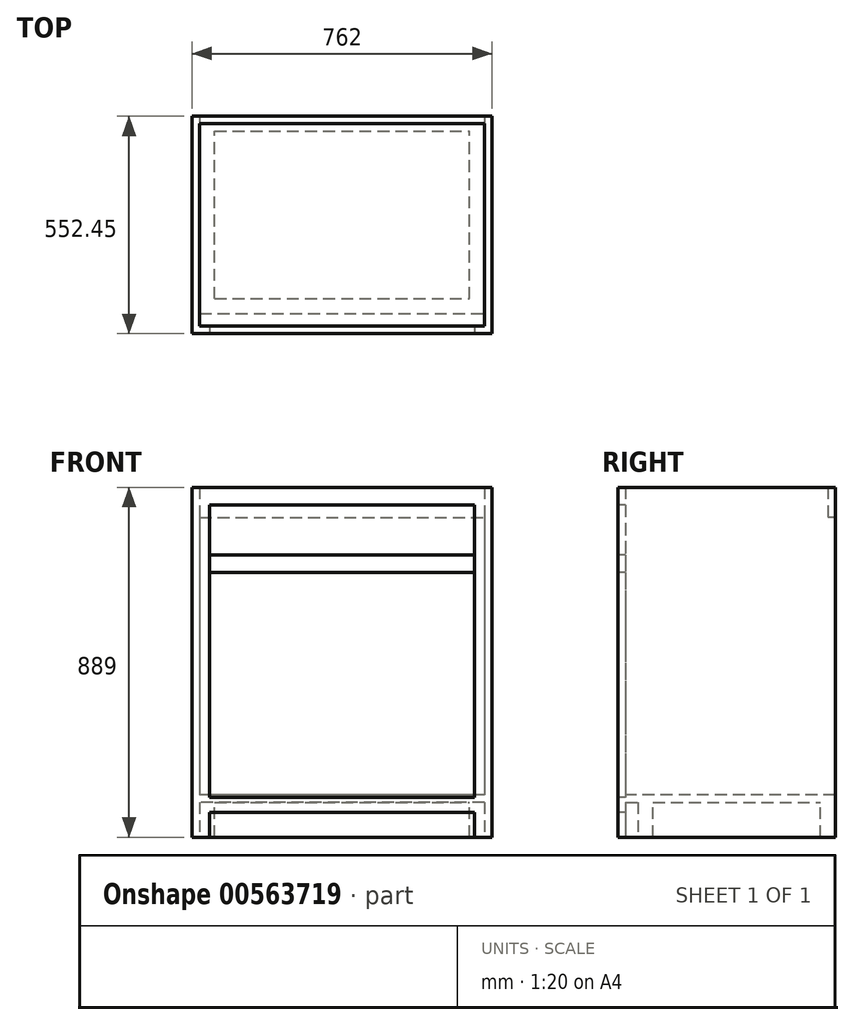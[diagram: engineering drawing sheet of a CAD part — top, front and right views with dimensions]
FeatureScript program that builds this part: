
annotation { "Feature Type Name" : "Feature", "Feature Type Description" : "" }
export const myFeature = defineFeature(function(context is Context, id is Id, definition is map)
    precondition{}
    {
        {
            var Q0;
            Q0=qCreatedBy(makeId("Front.planeOp"),FACE);
            var sketch = newSketch(context, id + "F0", { "sketchPlane" : qUnion([Q0])});
            skLineSegment(sketch, "E0.bottom", {"start": v(-76.53, 47.04) * mm, "end": v(-62.72, 47.04) * mm});
            skLineSegment(sketch, "E0.top", {"start": v(-76.53, -75.78) * mm, "end": v(-62.72, -75.78) * mm});
            skLineSegment(sketch, "E0.left", {"start": v(-76.53, 47.04) * mm, "end": v(-76.53, -75.78) * mm});
            skLineSegment(sketch, "E0.right", {"start": v(-62.72, 47.04) * mm, "end": v(-62.72, -75.78) * mm});
            skLineSegment(sketch, "E1.bottom", {"start": v(-189.83, 884.07) * mm, "end": v(-145.38, 884.07) * mm});
            skLineSegment(sketch, "E1.top", {"start": v(-189.83, -4.93) * mm, "end": v(-145.38, -4.93) * mm});
            skLineSegment(sketch, "E1.left", {"start": v(-189.83, 884.07) * mm, "end": v(-189.83, -4.93) * mm});
            skLineSegment(sketch, "E1.right", {"start": v(-145.38, 884.07) * mm, "end": v(-145.38, -4.93) * mm});
            skLineSegment(sketch, "E2.bottom", {"start": v(527.72, 884.07) * mm, "end": v(572.17, 884.07) * mm});
            skLineSegment(sketch, "E2.top", {"start": v(527.72, -4.93) * mm, "end": v(572.17, -4.93) * mm});
            skLineSegment(sketch, "E2.left", {"start": v(527.72, 884.07) * mm, "end": v(527.72, -4.93) * mm});
            skLineSegment(sketch, "E2.right", {"start": v(572.17, 884.07) * mm, "end": v(572.17, -4.93) * mm});
            skLineSegment(sketch, "E3", {"start": v(-145.38, 884.07) * mm, "end": v(527.72, 884.07) * mm});
            skLineSegment(sketch, "E4", {"start": v(-145.38, 839.62) * mm, "end": v(527.72, 839.62) * mm});
            skLineSegment(sketch, "E5", {"start": v(-145.38, 58.57) * mm, "end": v(527.72, 58.57) * mm});
            skLineSegment(sketch, "E6", {"start": v(-145.38, 96.67) * mm, "end": v(527.72, 96.67) * mm});
            skLineSegment(sketch, "E7.bottom", {"start": v(-145.38, 712.62) * mm, "end": v(527.72, 712.62) * mm});
            skLineSegment(sketch, "E7.top", {"start": v(-145.38, 668.17) * mm, "end": v(527.72, 668.17) * mm});
            skLineSegment(sketch, "E7.left", {"start": v(-145.38, 712.62) * mm, "end": v(-145.38, 668.17) * mm});
            skLineSegment(sketch, "E7.right", {"start": v(527.72, 712.62) * mm, "end": v(527.72, 668.17) * mm});
            skSolve(sketch);
        }
        {
            var Q0;
            {var subQ0=sQuery(id+"F0.wireOp",EDGE,"E5");Q0=makeQuery(id+"F0.imprint","IMPRINT",FACE,{"disambiguationData":[TD([[makeQuery(id+"F0.imprint","IMPRINT",EDGE,{"derivedFrom":subQ0}),1.0]])]});}
            var Q1;
            {var subQ1=sQuery(id+"F0.wireOp",EDGE,"E1.bottom");Q1=makeQuery(id+"F0.imprint","IMPRINT",FACE,{"disambiguationData":[TD([[makeQuery(id+"F0.imprint","IMPRINT",EDGE,{"derivedFrom":subQ1}),-1.0]])]});}
            var Q2;
            {var subQ0=sQuery(id+"F0.wireOp",EDGE,"E3");Q2=makeQuery(id+"F0.imprint","IMPRINT",FACE,{"disambiguationData":[TD([[makeQuery(id+"F0.imprint","IMPRINT",EDGE,{"derivedFrom":subQ0}),-1.0]])]});}
            var Q3;
            {var subQ3=sQuery(id+"F0.wireOp",EDGE,"E2.bottom");Q3=makeQuery(id+"F0.imprint","IMPRINT",FACE,{"disambiguationData":[TD([[makeQuery(id+"F0.imprint","IMPRINT",EDGE,{"derivedFrom":subQ3}),-1.0]])]});}
            extrude(context, id + "F1", {"entities" : qUnion([Q0, Q1, Q2, Q3]), "oppositeDirection" : true, "depth" : 19.05 * mm, "offsetDistance" : 25.4 * mm});
        }
        {
            var Q0;
            Q0=makeQuery(id+"F1.opExtrude","CAP_FACE",FACE,{"disambiguationData":[OSD([sQuery(id+"F0.wireOp",EDGE,"E1.bottom"),sQuery(id+"F0.wireOp",EDGE,"E1.top"),sQuery(id+"F0.wireOp",EDGE,"E1.left"),sQuery(id+"F0.wireOp",EDGE,"E1.right"),sQuery(id+"F0.wireOp",EDGE,"E2.bottom"),sQuery(id+"F0.wireOp",EDGE,"E2.top"),sQuery(id+"F0.wireOp",EDGE,"E2.left"),sQuery(id+"F0.wireOp",EDGE,"E2.right"),sQuery(id+"F0.wireOp",EDGE,"E3"),sQuery(id+"F0.wireOp",EDGE,"E4"),sQuery(id+"F0.wireOp",EDGE,"E5"),sQuery(id+"F0.wireOp",EDGE,"E6")])],"isStart":false});
            var sketch = newSketch(context, id + "F2", { "sketchPlane" : qUnion([Q0])});
            skLineSegment(sketch, "E8.bottom", {"start": v(-572.17, 884.07) * mm, "end": v(-553.12, 884.07) * mm});
            skLineSegment(sketch, "E8.top", {"start": v(-572.17, -4.93) * mm, "end": v(-553.12, -4.93) * mm});
            skLineSegment(sketch, "E8.left", {"start": v(-572.17, 884.07) * mm, "end": v(-572.17, -4.93) * mm});
            skLineSegment(sketch, "E8.right", {"start": v(-553.12, 884.07) * mm, "end": v(-553.12, -4.93) * mm});
            skLineSegment(sketch, "E9.bottom", {"start": v(189.83, 884.07) * mm, "end": v(170.78, 884.07) * mm});
            skLineSegment(sketch, "E9.top", {"start": v(189.83, -4.93) * mm, "end": v(170.78, -4.93) * mm});
            skLineSegment(sketch, "E9.left", {"start": v(189.83, 884.07) * mm, "end": v(189.83, -4.93) * mm});
            skLineSegment(sketch, "E9.right", {"start": v(170.78, 884.07) * mm, "end": v(170.78, -4.93) * mm});
            skLineSegment(sketch, "E10.left", {"start": v(-553.12, -4.93) * mm, "end": v(-553.12, 83.97) * mm});
            skSolve(sketch);
        }
        {
            var Q0;
            Q0=makeQuery(id+"F2.imprint","IMPRINT",FACE,{"disambiguationData":[TD([[makeQuery(id+"F2.imprint","IMPRINT",EDGE,{"derivedFrom":sQuery(id+"F2.wireOp",EDGE,"E8.bottom")}),1.0]])]});
            var Q1;
            Q1=makeQuery(id+"F2.imprint","IMPRINT",FACE,{"disambiguationData":[TD([[makeQuery(id+"F2.imprint","IMPRINT",EDGE,{"derivedFrom":sQuery(id+"F2.wireOp",EDGE,"E9.bottom")}),1.0]])]});
            extrude(context, id + "F3", {"entities" : qUnion([Q0, Q1]), "operationType" : NewBodyOperationType.ADD, "depth" : 533.4 * mm, "offsetDistance" : 25.4 * mm});
        }
        {
            var Q0;
            Q0=makeQuery(id+"F3.opExtrude","SWEPT_FACE",FACE,{"disambiguationData":[OSD([sQuery(id+"F2.wireOp",EDGE,"E8.right"),sQuery(id+"F2.wireOp",EDGE,"E10.left")])]});
            var sketch = newSketch(context, id + "F4", { "sketchPlane" : qUnion([Q0])});
            skLineSegment(sketch, "E11.bottom", {"start": v(-552.45, -4.93) * mm, "end": v(-514.35, -4.93) * mm});
            skLineSegment(sketch, "E11.top", {"start": v(-552.45, 83.97) * mm, "end": v(-514.35, 83.97) * mm});
            skLineSegment(sketch, "E11.left", {"start": v(-552.45, -4.93) * mm, "end": v(-552.45, 83.97) * mm});
            skLineSegment(sketch, "E11.right", {"start": v(-514.35, -4.93) * mm, "end": v(-514.35, 83.97) * mm});
            skLineSegment(sketch, "E12.bottom", {"start": v(-88.9, 83.97) * mm, "end": v(-50.8, 83.97) * mm});
            skLineSegment(sketch, "E12.top", {"start": v(-88.9, -4.93) * mm, "end": v(-50.8, -4.93) * mm});
            skLineSegment(sketch, "E12.left", {"start": v(-88.9, 83.97) * mm, "end": v(-88.9, -4.93) * mm});
            skLineSegment(sketch, "E12.right", {"start": v(-50.8, 83.97) * mm, "end": v(-50.8, -4.93) * mm});
            skSolve(sketch);
        }
        {
            var Q0;
            Q0=makeQuery(id+"F4.imprint","IMPRINT",FACE,{"disambiguationData":[TD([[makeQuery(id+"F4.imprint","IMPRINT",EDGE,{"derivedFrom":sQuery(id+"F4.wireOp",EDGE,"E11.bottom")}),1.0]])]});
            var Q1;
            Q1=makeQuery(id+"F4.imprint","IMPRINT",FACE,{"disambiguationData":[TD([[makeQuery(id+"F4.imprint","IMPRINT",EDGE,{"derivedFrom":sQuery(id+"F4.wireOp",EDGE,"E12.bottom")}),-1.0]])]});
            var Q2;
            Q2=makeQuery(id+"F3.opExtrude","SWEPT_FACE",FACE,{"disambiguationData":[OSD([sQuery(id+"F2.wireOp",EDGE,"E9.right")])]});
            extrude(context, id + "F5", {"entities" : qUnion([Q0, Q1]), "operationType" : NewBodyOperationType.ADD, "endBound" : BoundingType.UP_TO_SURFACE, "depth" : 25.4 * mm, "endBoundEntityFace" : qUnion([Q2]), "offsetDistance" : 25.4 * mm});
        }
        {
            var Q0;
            Q0=makeQuery(id+"F3.opExtrude","SWEPT_FACE",FACE,{"disambiguationData":[OSD([sQuery(id+"F2.wireOp",EDGE,"E9.right")])]});
            var sketch = newSketch(context, id + "F6", { "sketchPlane" : qUnion([Q0])});
            skLineSegment(sketch, "E13.bottom", {"start": v(19.05, 103.02) * mm, "end": v(552.45, 103.02) * mm});
            skLineSegment(sketch, "E13.top", {"start": v(19.05, 83.97) * mm, "end": v(552.45, 83.97) * mm});
            skLineSegment(sketch, "E13.left", {"start": v(19.05, 103.02) * mm, "end": v(19.05, 83.97) * mm});
            skLineSegment(sketch, "E13.right", {"start": v(552.45, 103.02) * mm, "end": v(552.45, 83.97) * mm});
            skSolve(sketch);
        }
        {
            var Q0;
            Q0=makeQuery(id+"F6.imprint","IMPRINT",FACE,{"disambiguationData":[TD([[makeQuery(id+"F6.imprint","IMPRINT",EDGE,{"derivedFrom":sQuery(id+"F6.wireOp",EDGE,"E13.bottom")}),-1.0]])]});
            var Q1;
            Q1=makeQuery(id+"F3.opExtrude","SWEPT_FACE",FACE,{"disambiguationData":[OSD([sQuery(id+"F2.wireOp",EDGE,"E8.right"),sQuery(id+"F2.wireOp",EDGE,"E10.left")])]});
            extrude(context, id + "F7", {"entities" : qUnion([Q0]), "operationType" : NewBodyOperationType.ADD, "endBound" : BoundingType.UP_TO_SURFACE, "depth" : 25.4 * mm, "endBoundEntityFace" : qUnion([Q1]), "offsetDistance" : 25.4 * mm});
        }
        {
            var Q0;
            Q0=makeQuery(id+"F7.boolean.opBoolean","SPLIT",FACE,{"disambiguationData":[TD([makeQuery(id+"F5.opExtrude","SWEPT_FACE",FACE,{"disambiguationData":[OSD([sQuery(id+"F4.wireOp",EDGE,"E11.right")])]})])],"derivedFrom":makeQuery(id+"F7.opExtrude","SWEPT_FACE",FACE,{"disambiguationData":[OSD([sQuery(id+"F6.wireOp",EDGE,"E13.top")])]})});
            var sketch = newSketch(context, id + "F8", { "sketchPlane" : qUnion([Q0])});
            skLineSegment(sketch, "E14.bottom", {"start": v(-170.78, -88.9) * mm, "end": v(-132.68, -88.9) * mm});
            skLineSegment(sketch, "E14.top", {"start": v(-170.78, -514.35) * mm, "end": v(-132.68, -514.35) * mm});
            skLineSegment(sketch, "E14.left", {"start": v(-170.78, -88.9) * mm, "end": v(-170.78, -514.35) * mm});
            skLineSegment(sketch, "E14.right", {"start": v(-132.68, -88.9) * mm, "end": v(-132.68, -514.35) * mm});
            skLineSegment(sketch, "E15.bottom", {"start": v(553.12, -88.9) * mm, "end": v(515.02, -88.9) * mm});
            skLineSegment(sketch, "E15.top", {"start": v(553.12, -514.35) * mm, "end": v(515.02, -514.35) * mm});
            skLineSegment(sketch, "E15.left", {"start": v(553.12, -88.9) * mm, "end": v(553.12, -514.35) * mm});
            skLineSegment(sketch, "E15.right", {"start": v(515.02, -88.9) * mm, "end": v(515.02, -514.35) * mm});
            skSolve(sketch);
        }
        {
            var Q0;
            Q0=makeQuery(id+"F8.imprint","IMPRINT",FACE,{"disambiguationData":[TD([[makeQuery(id+"F8.imprint","IMPRINT",EDGE,{"derivedFrom":sQuery(id+"F8.wireOp",EDGE,"E14.bottom")}),-1.0]])]});
            var Q1;
            Q1=makeQuery(id+"F8.imprint","IMPRINT",FACE,{"disambiguationData":[TD([[makeQuery(id+"F8.imprint","IMPRINT",EDGE,{"derivedFrom":sQuery(id+"F8.wireOp",EDGE,"E15.bottom")}),-1.0]])]});
            extrude(context, id + "F9", {"entities" : qUnion([Q0, Q1]), "operationType" : NewBodyOperationType.ADD, "depth" : 88.9 * mm, "offsetDistance" : 25.4 * mm});
        }
        {
            var Q0;
            {var subQ2=sQuery(id+"F4.wireOp",EDGE,"E11.top");Q0=makeQuery(id+"F4.imprint","IMPRINT",FACE,{"disambiguationData":[TD([[makeQuery(id+"F4.imprint","IMPRINT",EDGE,{"derivedFrom":subQ2}),1.0]])]});}
            var sketch = newSketch(context, id + "F10", { "sketchPlane" : qUnion([Q0])});
            skSolve(sketch);
        }
        {
            var Q0;
            {var subQ2=sQuery(id+"F4.wireOp",EDGE,"E11.top");Q0=makeQuery(id+"F10.imprint","IMPRINT",FACE,{"disambiguationData":[TD([[makeQuery(id+"F10.imprint","IMPRINT",EDGE,{"derivedFrom":makeQuery(id+"F4.imprint","IMPRINT",EDGE,{"derivedFrom":subQ2})}),1.0]])]});}
            var sketch = newSketch(context, id + "F11", { "sketchPlane" : qUnion([Q0])});
            skLineSegment(sketch, "E16.bottom", {"start": v(-552.45, 884.07) * mm, "end": v(-533.4, 884.07) * mm});
            skLineSegment(sketch, "E16.top", {"start": v(-552.45, 807.87) * mm, "end": v(-533.4, 807.87) * mm});
            skLineSegment(sketch, "E16.left", {"start": v(-552.45, 884.07) * mm, "end": v(-552.45, 807.87) * mm});
            skLineSegment(sketch, "E16.right", {"start": v(-533.4, 884.07) * mm, "end": v(-533.4, 807.87) * mm});
            skSolve(sketch);
        }
        {
            var Q0;
            Q0=makeQuery(id+"F11.imprint","IMPRINT",FACE,{"disambiguationData":[TD([[makeQuery(id+"F11.imprint","IMPRINT",EDGE,{"derivedFrom":sQuery(id+"F11.wireOp",EDGE,"E16.bottom")}),-1.0]])]});
            var Q1;
            {var subQ0=sQuery(id+"F2.wireOp",EDGE,"E8.bottom");var subQ5=sQuery(id+"F2.wireOp",EDGE,"E9.right");Q1=makeQuery(id+"F7.boolean.opBoolean","SPLIT",FACE,{"disambiguationData":[TD([makeQuery(id+"F3.opExtrude","SWEPT_FACE",FACE,{"disambiguationData":[OSD([subQ0])]})])],"derivedFrom":makeQuery(id+"F3.opExtrude","SWEPT_FACE",FACE,{"disambiguationData":[OSD([subQ5])]})});}
            extrude(context, id + "F12", {"entities" : qUnion([Q0]), "operationType" : NewBodyOperationType.ADD, "endBound" : BoundingType.UP_TO_SURFACE, "depth" : 25.4 * mm, "endBoundEntityFace" : qUnion([Q1]), "offsetDistance" : 25.4 * mm});
        }
        {
            var Q0;
            Q0=makeQuery(id+"F0.imprint","IMPRINT",FACE,{"disambiguationData":[TD([[makeQuery(id+"F0.imprint","IMPRINT",EDGE,{"derivedFrom":sQuery(id+"F0.wireOp",EDGE,"E7.bottom")}),-1.0]])]});
            extrude(context, id + "F13", {"entities" : qUnion([Q0]), "oppositeDirection" : true, "depth" : 19.05 * mm, "offsetDistance" : 25.4 * mm});
        }
        {
            var Q0;
            {var subQ0=sQuery(id+"F0.wireOp",EDGE,"E4");Q0=makeQuery(id+"F0.imprint","IMPRINT",FACE,{"disambiguationData":[TD([[makeQuery(id+"F0.imprint","IMPRINT",EDGE,{"derivedFrom":subQ0}),-1.0]])]});}
            var Q1;
            {var subQ0=sQuery(id+"F0.wireOp",EDGE,"E6");Q1=makeQuery(id+"F0.imprint","IMPRINT",FACE,{"disambiguationData":[TD([[makeQuery(id+"F0.imprint","IMPRINT",EDGE,{"derivedFrom":subQ0}),1.0]])]});}
            extrude(context, id + "F14", {"entities" : qUnion([Q0, Q1]), "oppositeDirection" : true, "depth" : 19.05 * mm, "offsetDistance" : 25.4 * mm});
        }
    });
